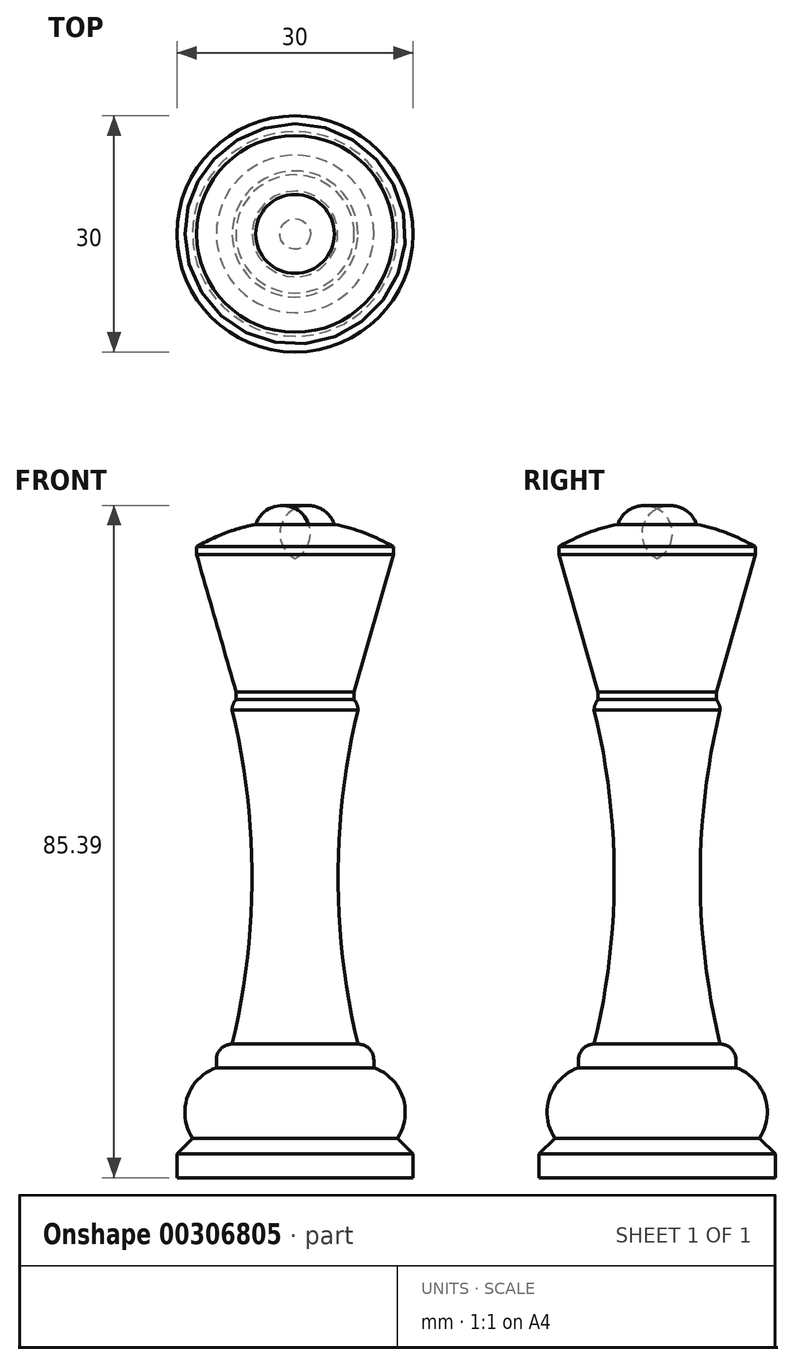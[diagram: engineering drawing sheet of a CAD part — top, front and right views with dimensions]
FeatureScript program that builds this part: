
annotation { "Feature Type Name" : "Feature", "Feature Type Description" : "" }
export const myFeature = defineFeature(function(context is Context, id is Id, definition is map)
    precondition{}
    {
        {
            var Q0;
            Q0=qCreatedBy(makeId("Front.planeOp"),FACE);
            var sketch = newSketch(context, id + "F0", { "sketchPlane" : qUnion([Q0])});
            skArc(sketch, "E0", {"start": v(12.5, -4.84) * mm, "mid": v(8.86, -3.12) * mm, "end": v(5, -2) * mm});
            skArc(sketch, "E1", {"start": v(5, -2) * mm, "mid": v(2.96, 0.14) * mm, "end": v(0, 0) * mm});
            skLineSegment(sketch, "E2", {"start": v(7.5, -23.28) * mm, "end": v(7.5, -24.28) * mm});
            skArc(sketch, "E3", {"start": v(8, -25.6) * mm, "mid": v(7.87, -24.9) * mm, "end": v(7.5, -24.28) * mm});
            skArc(sketch, "E4", {"start": v(8, -25.6) * mm, "mid": v(5.46, -46.82) * mm, "end": v(8, -68.03) * mm});
            skArc(sketch, "E5", {"start": v(10, -70.03) * mm, "mid": v(9.41, -68.62) * mm, "end": v(8, -68.03) * mm});
            skLineSegment(sketch, "E6", {"start": v(10, -70.03) * mm, "end": v(10, -71.03) * mm});
            skArc(sketch, "E7", {"start": v(13, -80) * mm, "mid": v(13.69, -74.78) * mm, "end": v(10, -71.03) * mm});
            skLineSegment(sketch, "E8", {"start": v(13, -80) * mm, "end": v(15, -82) * mm});
            skLineSegment(sketch, "E9", {"start": v(15, -82) * mm, "end": v(15, -85) * mm});
            skLineSegment(sketch, "E10", {"start": v(15, -85) * mm, "end": v(0, -85) * mm});
            skLineSegment(sketch, "E11", {"start": v(0, -85) * mm, "end": v(0, 0) * mm});
            skLineSegment(sketch, "E12", {"start": v(15, -82) * mm, "end": v(41.52, -82) * mm, "construction": true});
            skLineSegment(sketch, "E13", {"start": v(12.5, -4.84) * mm, "end": v(12.5, -5.84) * mm});
            skLineSegment(sketch, "E14", {"start": v(12.5, -5.84) * mm, "end": v(7.5, -23.28) * mm});
            skSolve(sketch);
        }
        {
            var Q0;
            Q0=makeQuery(id+"F0.imprint","IMPRINT",FACE,{"disambiguationData":[TD([[makeQuery(id+"F0.imprint","IMPRINT",EDGE,{"derivedFrom":sQuery(id+"F0.wireOp",EDGE,"E0")}),1.0]])]});
            var Q1;
            Q1=sQuery(id+"F0.wireOp",EDGE,"E11");
            revolve(context, id + "F1", {"entities" : qUnion([Q0]), "axis" : qUnion([Q1]), "revolveType" : RevolveType.FULL});
        }
    });
